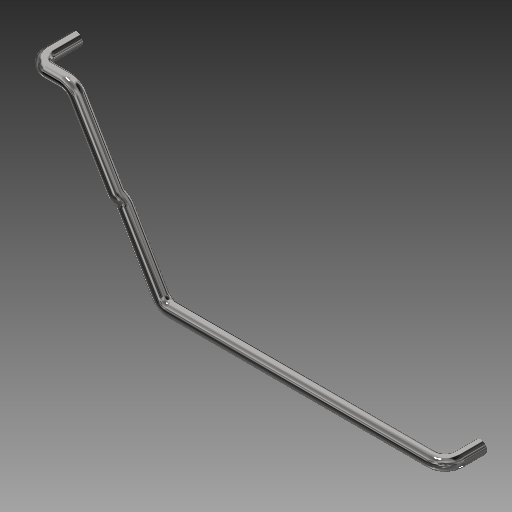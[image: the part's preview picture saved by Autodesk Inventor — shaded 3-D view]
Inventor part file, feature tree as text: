
AUTODESK INVENTOR PART (.ipt)
format: ipt  version: 2019 (Build 230136000, 136)  size: 189,952 bytes
history: native  units: mm
features: sketch x10, sweep x5, plane x5, other x5, projected_geometry x3
ambient origin geometry x8: Origin, YZ Plane, XZ Plane, XY Plane, X Axis, Y Axis, Z Axis, Center Point
bodies: Solid1 (feature_tree)
feature tree (28):
  sweep  "Sweep1"
  plane  "Work Plane1"
  sweep  "Sweep2"
  plane  "Work Plane2"
  sweep  "Sweep3"
  other  "Work Axis3"
  sketch  "Sketch7"  dims[d20=10.0mm]
  plane  "Work Plane3"
  sweep  "Sweep4"
  plane  "Work Plane4"
  sweep  "Sweep5"
  plane  "Work Plane5"
  sketch  "Sketch1"  dims[d0=4.76mm d1=13.0mm]
  sketch  "Sketch2"  dims[d2=100.0mm d3=5.0mm]
  other  "Work Axis1"
  sketch  "Sketch3"  dims[d4=0.0mm d5=90.0deg]
  sketch  "Sketch4"  dims[d6=10.0mm d11=35.0mm]
  other  "Work Axis2"
  sketch  "Sketch5"  dims[d12=0.0mm d13=90.0deg]
  sketch  "Sketch6"  dims[d16=10.0mm]
  projected_geometry  "Projected Loop1"
  sketch  "Sketch8"  dims[d21=0.0mm]
  projected_geometry  "Projected Loop2"
  other  "Work Axis4"
  sketch  "Sketch10"  dims[d22=1.2mm]
  sketch  "Sketch11"  dims[d23=15.0mm d24=0.0mm d27=5.0mm d28=5.0mm d29=0.0mm d30=90.0deg d33=5.0mm d34=15.0mm d35=0.0mm d40=90.0deg d41=27.027609mm d42=11.942844mm d43=5.0mm d44=54.620592mm d45=35.0mm d46=0.0mm d47=0.0mm d48=0.0mm d49=0.0mm d50=0.0mm]
  projected_geometry  "Projected Loop4"
  other  "Work Axis5"
